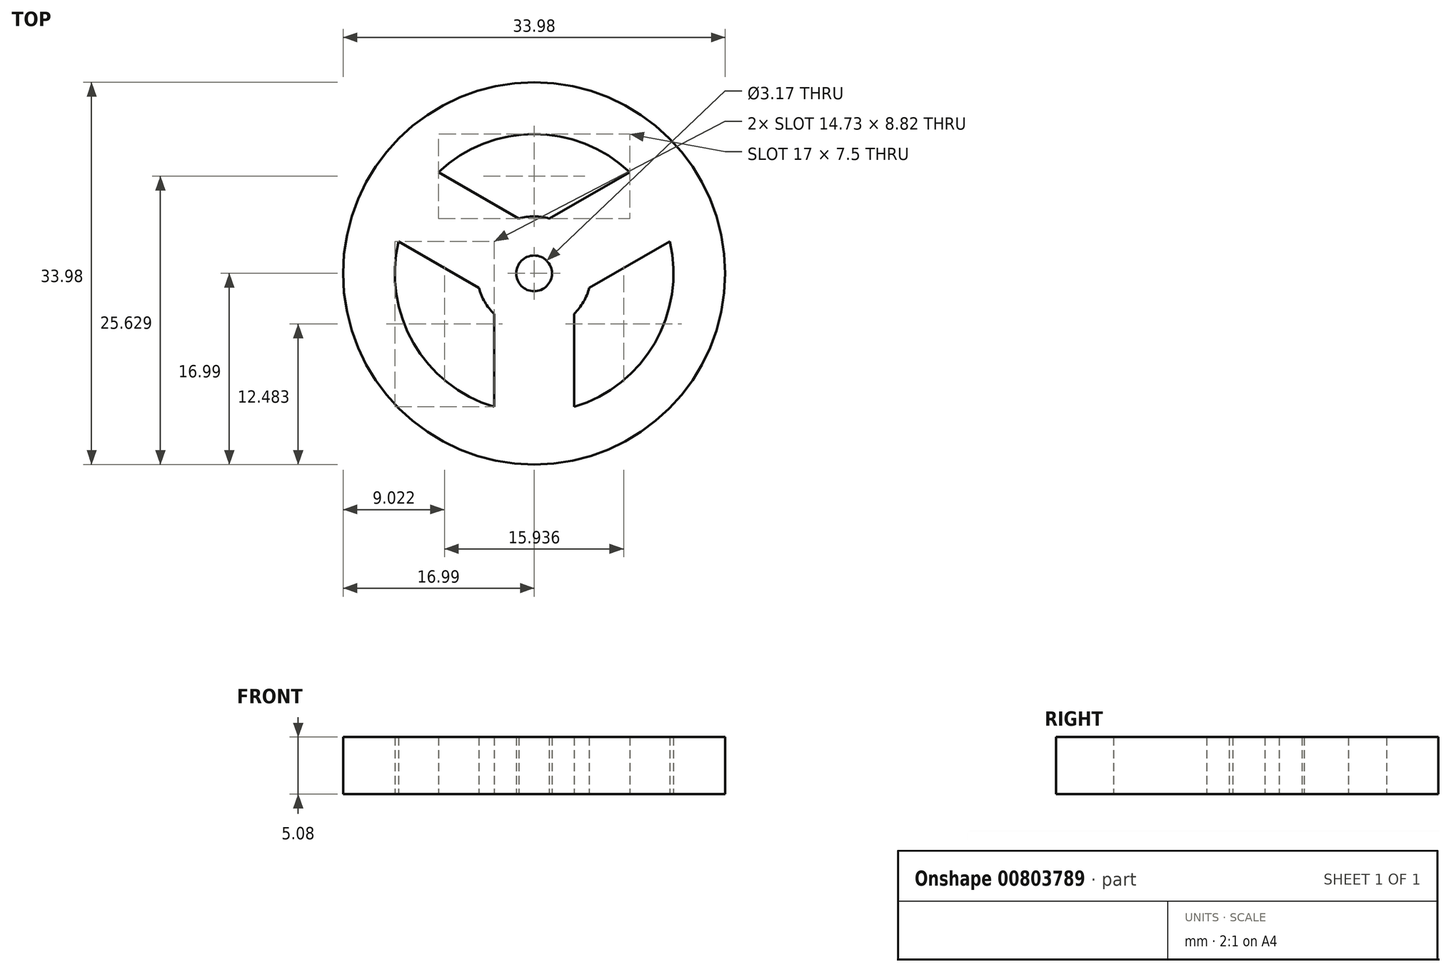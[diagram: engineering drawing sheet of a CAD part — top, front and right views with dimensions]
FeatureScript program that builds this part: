
annotation { "Feature Type Name" : "Feature", "Feature Type Description" : "" }
export const myFeature = defineFeature(function(context is Context, id is Id, definition is map)
    precondition{}
    {
        {
            var Q0;
            Q0=qCreatedBy(makeId("Top.planeOp"),FACE);
            var sketch = newSketch(context, id + "F0", { "sketchPlane" : qUnion([Q0])});
            skCircle(sketch, "E0", {"center": v(0, 0) * mm, "radius": 17 * mm});
            skCircle(sketch, "E1", {"center": v(0, 0) * mm, "radius": 1.59 * mm});
            skCircle(sketch, "E2", {"center": v(0, 0) * mm, "radius": 12.4 * mm});
            skCircle(sketch, "E3", {"center": v(0, 0) * mm, "radius": 5.07 * mm});
            skLineSegment(sketch, "E4", {"start": v(-3.56, -3.61) * mm, "end": v(-3.56, -11.87) * mm});
            skLineSegment(sketch, "E5", {"start": v(3.56, -3.61) * mm, "end": v(3.56, -11.87) * mm});
            skLineSegment(sketch, "E6.1.0", {"start": v(-1.35, 4.89) * mm, "end": v(-8.5, 9.01) * mm});
            skLineSegment(sketch, "E6.1.1", {"start": v(-4.9, -1.27) * mm, "end": v(-12.06, 2.86) * mm});
            skLineSegment(sketch, "E6.2.0", {"start": v(4.9, -1.27) * mm, "end": v(12.06, 2.86) * mm});
            skLineSegment(sketch, "E6.2.1", {"start": v(1.35, 4.89) * mm, "end": v(8.5, 9.01) * mm});
            skSolve(sketch);
        }
        {
            var Q0;
            Q0=makeQuery(id+"F0.imprint","IMPRINT",FACE,{"disambiguationData":[TD([[makeQuery(id+"F0.imprint","IMPRINT",EDGE,{"derivedFrom":sQuery(id+"F0.wireOp",EDGE,"E0")}),1.0]])]});
            var Q1;
            {var subQ0=sQuery(id+"F0.wireOp",EDGE,"E6.1.0");Q1=makeQuery(id+"F0.imprint","IMPRINT",FACE,{"disambiguationData":[TD([[makeQuery(id+"F0.imprint","IMPRINT",EDGE,{"derivedFrom":subQ0}),1.0]])]});}
            var Q2;
            Q2=makeQuery(id+"F0.imprint","IMPRINT",FACE,{"disambiguationData":[TD([[makeQuery(id+"F0.imprint","IMPRINT",EDGE,{"derivedFrom":sQuery(id+"F0.wireOp",EDGE,"E1")}),-1.0]])]});
            var Q3;
            {var subQ0=sQuery(id+"F0.wireOp",EDGE,"E4");Q3=makeQuery(id+"F0.imprint","IMPRINT",FACE,{"disambiguationData":[TD([[makeQuery(id+"F0.imprint","IMPRINT",EDGE,{"derivedFrom":subQ0}),1.0]])]});}
            var Q4;
            {var subQ0=sQuery(id+"F0.wireOp",EDGE,"E6.2.0");Q4=makeQuery(id+"F0.imprint","IMPRINT",FACE,{"disambiguationData":[TD([[makeQuery(id+"F0.imprint","IMPRINT",EDGE,{"derivedFrom":subQ0}),1.0]])]});}
            extrude(context, id + "F1", {"entities" : qUnion([Q0, Q1, Q2, Q3, Q4]), "depth" : 5.08 * mm, "offsetDistance" : 25.4 * mm});
        }
    });
